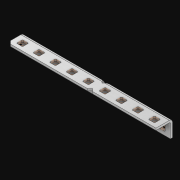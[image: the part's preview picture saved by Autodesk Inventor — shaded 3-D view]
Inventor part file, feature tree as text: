
AUTODESK INVENTOR PART (.ipt)
format: ipt  version: 2021 (Build 250183000, 183)  size: 607,232 bytes
history: native  units: in
note: dims shown in document units (in); Inventor stores cm internally (conversion verified against a paired STEP export)
features: extrude x19, other x18, sketch x3, pattern_linear x1, sheet_metal_op x1
ambient origin geometry x8: Origin, YZ Plane, XZ Plane, XY Plane, X Axis, Y Axis, Z Axis, Center Point
bodies: Solid1 (feature_tree)
feature tree (42):
  pattern_linear  "Rectangular Pattern1"  Spacing1=0.063in  [1 undecoded]
  extrude  "Extrusion1"  Depth=0.5in
  sketch  "Sketch1"  dims[d0=0.182in]
  other  "Srf1"
  sketch  "Sketch2"  dims[d1=0.063in d2=0.0in]
  other  "Srf2"
  other  "Srf3"
  other  "Srf5"
  other  "Srf7"
  other  "Srf9"
  other  "Srf11"
  other  "Srf13"
  other  "Srf15"
  other  "Srf17"
  other  "Srf4"
  other  "Srf6"
  other  "Srf8"
  other  "Srf10"
  other  "Srf12"
  other  "Srf14"
  other  "Srf16"
  other  "Srf18"
  sketch  "Sketch3"  dims[d3=0.182in d4=0.063in d5=0.0in d8=0.5in d9=13.0in d10=0.0in]
  sheet_metal_op  "Fold1"
  extrude  "ExtrusionSrf1"  Depth=0.5in TaperAngle=0.0deg
  extrude  "ExtrusionSrf2"  [1 undecoded]
  extrude  "ExtrusionSrf3"  [1 undecoded]
  extrude  "ExtrusionSrf4"  [1 undecoded]
  extrude  "ExtrusionSrf5"  [1 undecoded]
  extrude  "ExtrusionSrf6"  [1 undecoded]
  extrude  "ExtrusionSrf7"  [1 undecoded]
  extrude  "ExtrusionSrf8"  [1 undecoded]
  extrude  "ExtrusionSrf9"  [1 undecoded]
  extrude  "ExtrusionSrf10"  [1 undecoded]
  extrude  "ExtrusionSrf37"  [1 undecoded]
  extrude  "ExtrusionSrf38"  [1 undecoded]
  extrude  "ExtrusionSrf39"  [1 undecoded]
  extrude  "ExtrusionSrf40"  [1 undecoded]
  extrude  "ExtrusionSrf41"  [1 undecoded]
  extrude  "ExtrusionSrf42"  [1 undecoded]
  extrude  "ExtrusionSrf43"  [1 undecoded]
  extrude  "ExtrusionSrf44"  [1 undecoded]
note: 18 required parameter values undecoded (feature->parameter linkage not recoverable at this tier; creation-order binding heuristic only, values carry confidence <= 0.55)
